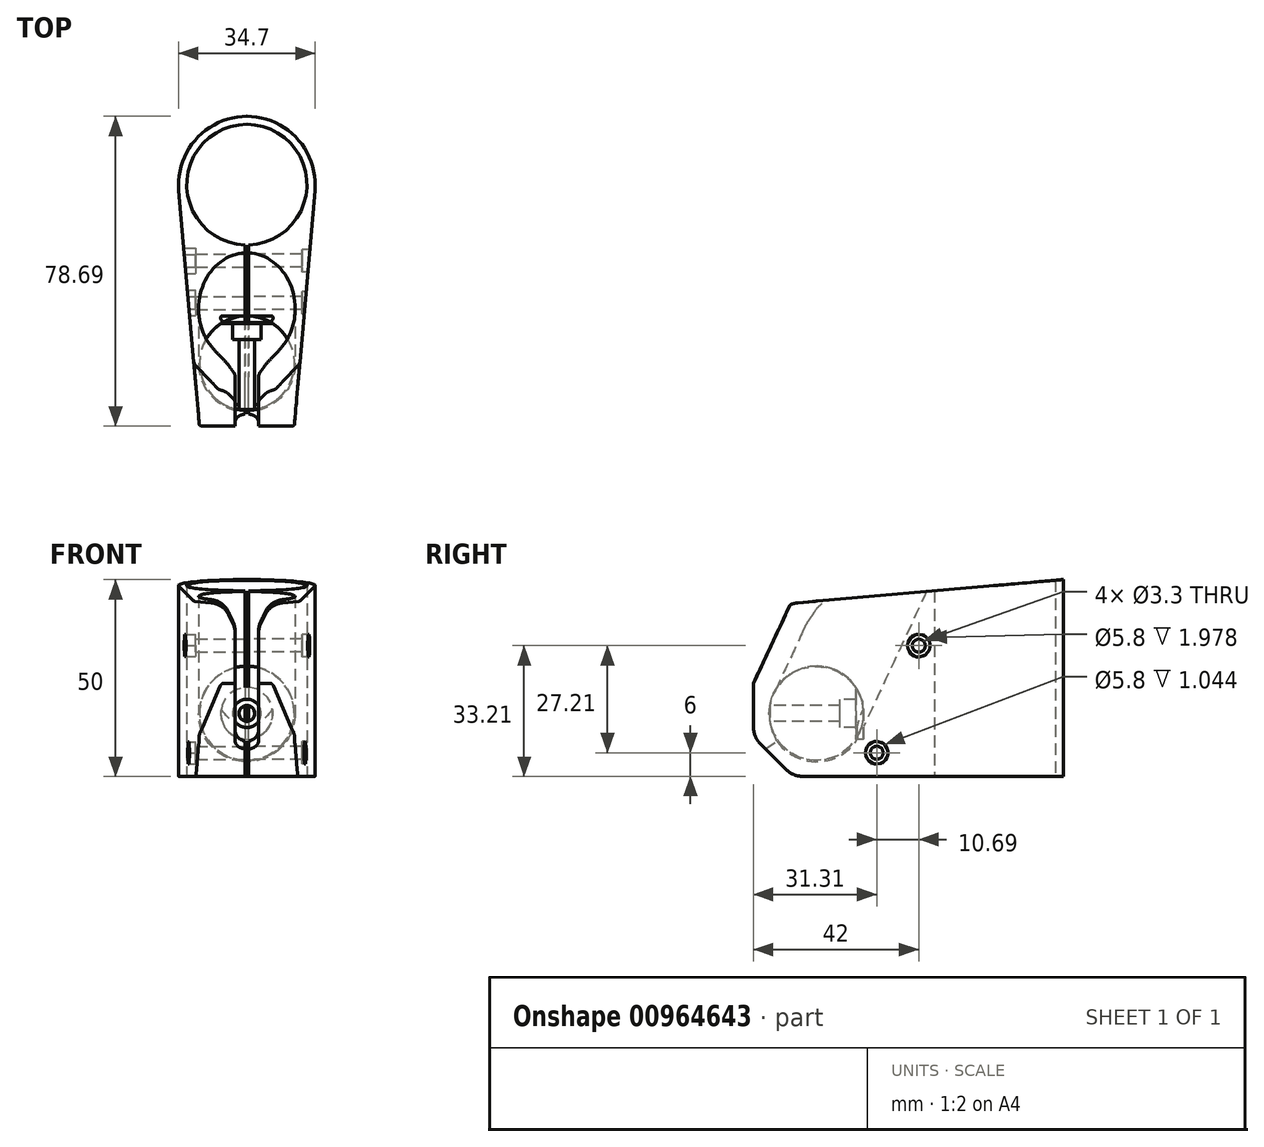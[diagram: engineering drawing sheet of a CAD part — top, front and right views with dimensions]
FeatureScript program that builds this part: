
annotation { "Feature Type Name" : "Feature", "Feature Type Description" : "" }
export const myFeature = defineFeature(function(context is Context, id is Id, definition is map)
    precondition{}
    {
        {
            var Q0;
            Q0=qCreatedBy(makeId("Top.planeOp"),FACE);
            var sketch = newSketch(context, id + "F0", { "sketchPlane" : qUnion([Q0])});
            skCircle(sketch, "E0", {"center": v(0, 0) * mm, "radius": 15.35 * mm, "construction": true});
            skSolve(sketch);
        }
        {
            var Q0;
            Q0=qCreatedBy(makeId("Top.planeOp"),FACE);
            var sketch = newSketch(context, id + "F1", { "sketchPlane" : qUnion([Q0])});
            skArc(sketch, "E1", {"start": v(0.5, -15.34) * mm, "mid": v(15.35, 0.25) * mm, "end": v(0, 15.35) * mm});
            skLineSegment(sketch, "E2", {"start": v(0.5, -15.34) * mm, "end": v(0.5, -61.34) * mm});
            skLineSegment(sketch, "E3", {"start": v(0.5, -61.34) * mm, "end": v(12.05, -61.34) * mm});
            skLineSegment(sketch, "E4", {"start": v(12.05, -61.34) * mm, "end": v(17.28, -1.51) * mm});
            skLineSegment(sketch, "E5", {"start": v(0, 0) * mm, "end": v(0, 15.35) * mm, "construction": true});
            skArc(sketch, "E6", {"start": v(17.28, -1.51) * mm, "mid": v(12.8, 11.72) * mm, "end": v(0, 17.35) * mm});
            skLineSegment(sketch, "E7", {"start": v(0, 15.35) * mm, "end": v(0, 17.35) * mm});
            skSolve(sketch);
        }
        {
            var Q0;
            Q0=qSketchRegion(id+"F1",true);
            extrude(context, id + "F2", {"entities" : qUnion([Q0]), "depth" : 50 * mm});
        }
        {
            var Q0;
            Q0=qCreatedBy(makeId("Right.planeOp"),FACE);
            var sketch = newSketch(context, id + "F3", { "sketchPlane" : qUnion([Q0])});
            skLineSegment(sketch, "E8", {"start": v(-22.2, 65.65) * mm, "end": v(-50.54, 4.85) * mm});
            skArc(sketch, "E9", {"start": v(-56.49, 21.2) * mm, "mid": v(-56.9, 11.8) * mm, "end": v(-50.54, 4.85) * mm});
            skLineSegment(sketch, "E10", {"start": v(-56.49, 21.2) * mm, "end": v(-33.34, 70.84) * mm});
            skLineSegment(sketch, "E11", {"start": v(-33.34, 70.84) * mm, "end": v(-22.2, 65.65) * mm});
            skSolve(sketch);
        }
        {
            var Q0;
            Q0=qSketchRegion(id+"F3",true);
            var Q1;
            Q1=sQuery(id+"F3.wireOp",EDGE,"E8");
            revolve(context, id + "F4", {"operationType" : NewBodyOperationType.REMOVE, "entities" : qUnion([Q0]), "axis" : qUnion([Q1]), "revolveType" : RevolveType.FULL});
        }
        {
            var Q0;
            Q0=makeQuery(id+"F2.opExtrude","CAP_EDGE",EDGE,{"disambiguationData":[OSD([sQuery(id+"F1.wireOp",EDGE,"E3")])],"isStart":true});
            chamfer(context, id + "F5", {"entities" : qUnion([Q0]), "width" : 10 * mm, "tangentPropagation" : true});
        }
        {
            var Q0;
            Q0=qCreatedBy(makeId("Right.planeOp"),FACE);
            var sketch = newSketch(context, id + "F6", { "sketchPlane" : qUnion([Q0])});
            skCircle(sketch, "E12", {"center": v(-19.34, 33.21) * mm, "radius": 1.65 * mm});
            skCircle(sketch, "E13", {"center": v(-30.03, 6) * mm, "radius": 1.65 * mm});
            skLineSegment(sketch, "E14", {"start": v(-30.03, 6) * mm, "end": v(-19.34, 33.21) * mm, "construction": true});
            skLineSegment(sketch, "E15", {"start": v(-30.03, 6) * mm, "end": v(-30.03, 0) * mm, "construction": true});
            skLineSegment(sketch, "E16", {"start": v(-30.03, 6) * mm, "end": v(-35.05, 9.28) * mm, "construction": true});
            skLineSegment(sketch, "E17", {"start": v(-19.34, 33.21) * mm, "end": v(-22.97, 34.9) * mm, "construction": true});
            skLineSegment(sketch, "E18", {"start": v(-19.34, 33.21) * mm, "end": v(-15.34, 33.21) * mm, "construction": true});
            skLineSegment(sketch, "E19", {"start": v(-35.05, 9.28) * mm, "end": v(-31.35, 14.95) * mm, "construction": true});
            skSolve(sketch);
        }
        {
            var Q0;
            Q0=qSketchRegion(id+"F6",true);
            extrude(context, id + "F7", {"entities" : qUnion([Q0]), "operationType" : NewBodyOperationType.REMOVE, "endBound" : BoundingType.THROUGH_ALL, "depth" : 25 * mm});
        }
        {
            var Q0;
            Q0=qCreatedBy(makeId("Right.planeOp"),FACE);
            var sketch = newSketch(context, id + "F8", { "sketchPlane" : qUnion([Q0])});
            skLineSegment(sketch, "E20", {"start": v(-61.34, 50) * mm, "end": v(-49.05, 50) * mm});
            skLineSegment(sketch, "E21", {"start": v(-49.05, 50) * mm, "end": v(-61.34, 23.64) * mm});
            skLineSegment(sketch, "E22", {"start": v(-61.34, 23.64) * mm, "end": v(-61.34, 50) * mm});
            skLineSegment(sketch, "E23", {"start": v(-43.05, 50) * mm, "end": v(-49.05, 50) * mm, "construction": true});
            skSolve(sketch);
        }
        {
            var Q0;
            Q0=qSketchRegion(id+"F8",true);
            extrude(context, id + "F9", {"entities" : qUnion([Q0]), "operationType" : NewBodyOperationType.REMOVE, "endBound" : BoundingType.THROUGH_ALL, "depth" : 25 * mm});
        }
        {
            var Q0;
            Q0=qCreatedBy(makeId("Right.planeOp"),FACE);
            var sketch = newSketch(context, id + "F10", { "sketchPlane" : qUnion([Q0])});
            skLineSegment(sketch, "E24", {"start": v(-29.49, 50) * mm, "end": v(-45.34, 16) * mm});
            skLineSegment(sketch, "E25", {"start": v(-45.34, 16) * mm, "end": v(-74.39, -4.34) * mm});
            skLineSegment(sketch, "E26", {"start": v(-74.39, -4.34) * mm, "end": v(-49.05, 50) * mm});
            skLineSegment(sketch, "E27", {"start": v(-49.05, 50) * mm, "end": v(-29.49, 50) * mm});
            skSolve(sketch);
        }
        {
            var Q0;
            Q0=qSketchRegion(id+"F10",true);
            extrude(context, id + "F11", {"entities" : qUnion([Q0]), "operationType" : NewBodyOperationType.REMOVE, "endBound" : BoundingType.SYMMETRIC, "depth" : 6 * mm});
        }
        {
            var Q0;
            Q0=makeQuery(id+"F11.boolean.opBoolean","COPY",EDGE,{"derivedFrom":makeQuery(id+"F11.opExtrude","CAP_EDGE",EDGE,{"disambiguationData":[OSD([sQuery(id+"F10.wireOp",EDGE,"E25")])],"isStart":false})});
            fillet(context, id + "F12", {"entities" : qUnion([Q0]), "radius" : 3 * mm, "tangentPropagation" : true, "allowEdgeOverflow" : false});
        }
        {
            var Q0;
            Q0=makeQuery(id+"F9.boolean.opBoolean","COPY",EDGE,{"derivedFrom":makeQuery(id+"F9.opExtrude","SWEPT_EDGE",EDGE,{"disambiguationData":[OSD([sQuery(id+"F8.wireOp",EDGE,"E21"),sQuery(id+"F8.wireOp",EDGE,"E22")])]})});
            var Q1;
            {var subQ0=sQuery(id+"F1.wireOp",EDGE,"E3");Q1=makeQuery(id+"F5.opChamfer","BLEND_EDGE",EDGE,{"blendedFrom":[makeQuery(id+"F2.opExtrude","CAP_EDGE",EDGE,{"disambiguationData":[OSD([subQ0])],"isStart":true}),makeQuery(id+"F2.opExtrude","SWEPT_FACE",FACE,{"disambiguationData":[OSD([subQ0])]})],"blendedInto":[makeQuery(id+"F2.opExtrude","SWEPT_FACE",FACE,{"disambiguationData":[OSD([subQ0])]})]});}
            var Q2;
            {var subQ0=sQuery(id+"F1.wireOp",EDGE,"E3");Q2=makeQuery(id+"F5.opChamfer","BLEND_EDGE",EDGE,{"blendedFrom":[makeQuery(id+"F2.opExtrude","CAP_EDGE",EDGE,{"disambiguationData":[OSD([subQ0])],"isStart":true}),makeQuery(id+"F2.opExtrude","CAP_FACE",FACE,{"disambiguationData":[OSD([sQuery(id+"F1.wireOp",EDGE,"E1"),sQuery(id+"F1.wireOp",EDGE,"E2"),subQ0,sQuery(id+"F1.wireOp",EDGE,"E4"),sQuery(id+"F1.wireOp",EDGE,"E6"),sQuery(id+"F1.wireOp",EDGE,"E7")])],"isStart":true})],"blendedInto":[makeQuery(id+"F2.opExtrude","CAP_FACE",FACE,{"disambiguationData":[OSD([sQuery(id+"F1.wireOp",EDGE,"E1"),sQuery(id+"F1.wireOp",EDGE,"E2"),subQ0,sQuery(id+"F1.wireOp",EDGE,"E4"),sQuery(id+"F1.wireOp",EDGE,"E6"),sQuery(id+"F1.wireOp",EDGE,"E7")])],"isStart":true})]});}
            fillet(context, id + "F13", {"entities" : qUnion([Q0, Q1, Q2]), "radius" : 6 * mm, "tangentPropagation" : true, "allowEdgeOverflow" : false});
        }
        {
            var Q0;
            Q0=makeQuery(id+"F2.opExtrude","SWEPT_BODY",BODY,{"disambiguationData":[OSD([sQuery(id+"F1.wireOp",EDGE,"E1"),sQuery(id+"F1.wireOp",EDGE,"E2"),sQuery(id+"F1.wireOp",EDGE,"E3"),sQuery(id+"F1.wireOp",EDGE,"E4"),sQuery(id+"F1.wireOp",EDGE,"E6"),sQuery(id+"F1.wireOp",EDGE,"E7")])]});
            var Q1;
            Q1=makeQuery(id+"F2.opExtrude","SWEPT_FACE",FACE,{"disambiguationData":[OSD([sQuery(id+"F1.wireOp",EDGE,"E7")])]});
            mirror(context, id + "F14", {"operationType" : NewBodyOperationType.ADD, "entities" : qUnion([Q0]), "mirrorPlane" : qUnion([Q1])});
        }
        {
            var Q0;
            Q0=makeQuery(id+"F14.opPattern","COPY",EDGE,{"derivedFrom":makeQuery(id+"F9.boolean.opBoolean","INTERSECT",EDGE,{"derivedFrom":[makeQuery(id+"F2.opExtrude","SWEPT_FACE",FACE,{"disambiguationData":[OSD([sQuery(id+"F1.wireOp",EDGE,"E4")])]}),makeQuery(id+"F9.opExtrude","SWEPT_FACE",FACE,{"disambiguationData":[OSD([sQuery(id+"F8.wireOp",EDGE,"E21")])]})]}),"instanceName":"1"});
            var Q1;
            Q1=makeQuery(id+"F9.boolean.opBoolean","INTERSECT",EDGE,{"derivedFrom":[makeQuery(id+"F2.opExtrude","SWEPT_FACE",FACE,{"disambiguationData":[OSD([sQuery(id+"F1.wireOp",EDGE,"E4")])]}),makeQuery(id+"F9.opExtrude","SWEPT_FACE",FACE,{"disambiguationData":[OSD([sQuery(id+"F8.wireOp",EDGE,"E21")])]})]});
            chamfer(context, id + "F15", {"entities" : qUnion([Q0, Q1]), "width" : 6 * mm});
        }
        {
            var Q0;
            Q0=qCreatedBy(makeId("Right.planeOp"),FACE);
            var sketch = newSketch(context, id + "F16", { "sketchPlane" : qUnion([Q0])});
            skLineSegment(sketch, "E28", {"start": v(-34.47, 10.93) * mm, "end": v(-56.22, 21.07) * mm});
            skArc(sketch, "E29", {"start": v(-56.22, 21.07) * mm, "mid": v(-50.41, 5.12) * mm, "end": v(-34.47, 10.93) * mm});
            skSolve(sketch);
        }
        {
            var Q0;
            Q0=qSketchRegion(id+"F16",true);
            var Q1;
            Q1=sQuery(id+"F16.wireOp",EDGE,"E28");
            revolve(context, id + "F17", {"entities" : qUnion([Q0]), "axis" : qUnion([Q1]), "revolveType" : RevolveType.FULL});
        }
        {
            var Q0;
            {var subQ0=makeQuery(id+"F2.opExtrude","CAP_EDGE",EDGE,{"disambiguationData":[OSD([sQuery(id+"F1.wireOp",EDGE,"E6")])],"isStart":true});Q0=makeQuery(id+"F14.boolean.opBoolean","MERGE",EDGE,{"derivedFrom":[subQ0,makeQuery(id+"F14.opPattern","COPY",EDGE,{"derivedFrom":subQ0,"instanceName":"1"})]});}
            var Q1;
            {var subQ0=makeQuery(id+"F2.opExtrude","SWEPT_FACE",FACE,{"disambiguationData":[OSD([sQuery(id+"F1.wireOp",EDGE,"E4")])]});Q1=makeQuery(id+"F15.opChamfer","BLEND_EDGE",EDGE,{"blendedFrom":[makeQuery(id+"F14.opPattern","COPY",EDGE,{"derivedFrom":makeQuery(id+"F9.boolean.opBoolean","INTERSECT",EDGE,{"derivedFrom":[subQ0,makeQuery(id+"F9.opExtrude","SWEPT_FACE",FACE,{"disambiguationData":[OSD([sQuery(id+"F8.wireOp",EDGE,"E21")])]})]}),"instanceName":"1"}),makeQuery(id+"F14.opPattern","COPY",FACE,{"derivedFrom":subQ0,"instanceName":"1"})],"blendedInto":[makeQuery(id+"F14.opPattern","COPY",FACE,{"derivedFrom":subQ0,"instanceName":"1"})]});}
            var Q2;
            {var subQ0=makeQuery(id+"F9.opExtrude","SWEPT_FACE",FACE,{"disambiguationData":[OSD([sQuery(id+"F8.wireOp",EDGE,"E21")])]});Q2=makeQuery(id+"F15.opChamfer","BLEND_EDGE",EDGE,{"blendedFrom":[makeQuery(id+"F14.opPattern","COPY",EDGE,{"derivedFrom":makeQuery(id+"F9.boolean.opBoolean","INTERSECT",EDGE,{"derivedFrom":[makeQuery(id+"F2.opExtrude","SWEPT_FACE",FACE,{"disambiguationData":[OSD([sQuery(id+"F1.wireOp",EDGE,"E4")])]}),subQ0]}),"instanceName":"1"}),makeQuery(id+"F14.opPattern","COPY",FACE,{"derivedFrom":makeQuery(id+"F9.boolean.opBoolean","COPY",FACE,{"derivedFrom":subQ0}),"instanceName":"1"})],"blendedInto":[makeQuery(id+"F14.opPattern","COPY",FACE,{"derivedFrom":makeQuery(id+"F9.boolean.opBoolean","COPY",FACE,{"derivedFrom":subQ0}),"instanceName":"1"})]});}
            var Q3;
            {var subQ0=makeQuery(id+"F9.opExtrude","SWEPT_FACE",FACE,{"disambiguationData":[OSD([sQuery(id+"F8.wireOp",EDGE,"E21")])]});Q3=makeQuery(id+"F15.opChamfer","BLEND_EDGE",EDGE,{"blendedFrom":[makeQuery(id+"F9.boolean.opBoolean","INTERSECT",EDGE,{"derivedFrom":[makeQuery(id+"F2.opExtrude","SWEPT_FACE",FACE,{"disambiguationData":[OSD([sQuery(id+"F1.wireOp",EDGE,"E4")])]}),subQ0]}),makeQuery(id+"F9.boolean.opBoolean","COPY",FACE,{"derivedFrom":subQ0})],"blendedInto":[makeQuery(id+"F9.boolean.opBoolean","COPY",FACE,{"derivedFrom":subQ0})]});}
            var Q4;
            {var subQ0=makeQuery(id+"F2.opExtrude","SWEPT_FACE",FACE,{"disambiguationData":[OSD([sQuery(id+"F1.wireOp",EDGE,"E4")])]});Q4=makeQuery(id+"F15.opChamfer","BLEND_EDGE",EDGE,{"blendedFrom":[makeQuery(id+"F9.boolean.opBoolean","INTERSECT",EDGE,{"derivedFrom":[subQ0,makeQuery(id+"F9.opExtrude","SWEPT_FACE",FACE,{"disambiguationData":[OSD([sQuery(id+"F8.wireOp",EDGE,"E21")])]})]}),subQ0],"blendedInto":[subQ0]});}
            fillet(context, id + "F18", {"entities" : qUnion([Q0, Q1, Q2, Q3, Q4]), "radius" : 1 * mm, "tangentPropagation" : true, "rho" : .2, "crossSection" : FilletCrossSection.CONIC, "allowEdgeOverflow" : false});
        }
        {
            var Q0;
            Q0=qCreatedBy(makeId("Right.planeOp"),FACE);
            var sketch = newSketch(context, id + "F19", { "sketchPlane" : qUnion([Q0])});
            skLineSegment(sketch, "E30", {"start": v(-33.34, 16) * mm, "end": v(-57.34, 16) * mm});
            skLineSegment(sketch, "E31", {"start": v(-57.34, 16) * mm, "end": v(-57.34, 18) * mm});
            skLineSegment(sketch, "E32", {"start": v(-57.34, 18) * mm, "end": v(-39.34, 18) * mm});
            skLineSegment(sketch, "E33", {"start": v(-39.34, 18) * mm, "end": v(-39.34, 19.6) * mm});
            skLineSegment(sketch, "E34", {"start": v(-33.34, 19.6) * mm, "end": v(-33.34, 16) * mm});
            skCircle(sketch, "E35", {"center": v(-45.34, 16) * mm, "radius": 12 * mm, "construction": true});
            skLineSegment(sketch, "E36", {"start": v(-39.34, 19.6) * mm, "end": v(-35.34, 19.6) * mm});
            skLineSegment(sketch, "E37", {"start": v(-35.34, 19.6) * mm, "end": v(-35.34, 22.63) * mm});
            skLineSegment(sketch, "E38", {"start": v(-35.34, 22.63) * mm, "end": v(-33.34, 22.63) * mm});
            skLineSegment(sketch, "E39", {"start": v(-33.34, 22.63) * mm, "end": v(-33.34, 19.6) * mm});
            skSolve(sketch);
        }
        {
            var Q0;
            Q0=qSketchRegion(id+"F19",true);
            var Q1;
            Q1=sQuery(id+"F19.wireOp",EDGE,"E30");
            revolve(context, id + "F20", {"operationType" : NewBodyOperationType.REMOVE, "entities" : qUnion([Q0]), "axis" : qUnion([Q1]), "revolveType" : RevolveType.FULL, "oppositeDirection" : true});
        }
        {
            var Q0;
            Q0=qCreatedBy(makeId("Right.planeOp"),FACE);
            var sketch = newSketch(context, id + "F21", { "sketchPlane" : qUnion([Q0])});
            skLineSegment(sketch, "E40", {"start": v(17.35, 50) * mm, "end": v(-84.6, 50) * mm});
            skLineSegment(sketch, "E41", {"start": v(-84.6, 50) * mm, "end": v(-84.6, 41.08) * mm});
            skLineSegment(sketch, "E42", {"start": v(-84.6, 41.08) * mm, "end": v(17.35, 50) * mm});
            skSolve(sketch);
        }
        {
            var Q0;
            Q0=qSketchRegion(id+"F21",true);
            extrude(context, id + "F22", {"entities" : qUnion([Q0]), "operationType" : NewBodyOperationType.REMOVE, "endBound" : BoundingType.THROUGH_ALL, "oppositeDirection" : true, "depth" : 25 * mm, "hasSecondDirection" : true, "secondDirectionBound" : SecondDirectionBoundingType.THROUGH_ALL, "secondDirectionOppositeDirection" : false, "secondDirectionDepth" : 25 * mm});
        }
        {
            var Q0;
            Q0=makeQuery(id+"F22.boolean.opBoolean","INTERSECT",EDGE,{"derivedFrom":[makeQuery(id+"F11.boolean.opBoolean","COPY",FACE,{"derivedFrom":makeQuery(id+"F11.opExtrude","CAP_FACE",FACE,{"disambiguationData":[OSD([sQuery(id+"F10.wireOp",EDGE,"E24"),sQuery(id+"F10.wireOp",EDGE,"E25"),sQuery(id+"F10.wireOp",EDGE,"E26"),sQuery(id+"F10.wireOp",EDGE,"E27")])],"isStart":false})}),makeQuery(id+"F22.opExtrude","SWEPT_FACE",FACE,{"disambiguationData":[OSD([sQuery(id+"F21.wireOp",EDGE,"E42")])]})]});
            var Q1;
            Q1=makeQuery(id+"F22.boolean.opBoolean","INTERSECT",EDGE,{"derivedFrom":[makeQuery(id+"F14.opPattern","COPY",FACE,{"derivedFrom":makeQuery(id+"F11.boolean.opBoolean","COPY",FACE,{"derivedFrom":makeQuery(id+"F11.opExtrude","CAP_FACE",FACE,{"disambiguationData":[OSD([sQuery(id+"F10.wireOp",EDGE,"E24"),sQuery(id+"F10.wireOp",EDGE,"E25"),sQuery(id+"F10.wireOp",EDGE,"E26"),sQuery(id+"F10.wireOp",EDGE,"E27")])],"isStart":false})}),"instanceName":"1"}),makeQuery(id+"F22.opExtrude","SWEPT_FACE",FACE,{"disambiguationData":[OSD([sQuery(id+"F21.wireOp",EDGE,"E42")])]})]});
            chamfer(context, id + "F23", {"entities" : qUnion([Q0, Q1]), "chamferType" : ChamferType.TWO_OFFSETS, "width1" : 6 * mm, "oppositeDirection" : false, "width2" : 3 * mm, "tangentPropagation" : true});
        }
        {
            var Q0;
            {var subQ0=makeQuery(id+"F22.opExtrude","SWEPT_FACE",FACE,{"disambiguationData":[OSD([sQuery(id+"F21.wireOp",EDGE,"E42")])]});Q0=makeQuery(id+"F23.opChamfer","BLEND_EDGE",EDGE,{"blendedFrom":[makeQuery(id+"F22.boolean.opBoolean","INTERSECT",EDGE,{"derivedFrom":[makeQuery(id+"F11.boolean.opBoolean","COPY",FACE,{"derivedFrom":makeQuery(id+"F11.opExtrude","CAP_FACE",FACE,{"disambiguationData":[OSD([sQuery(id+"F10.wireOp",EDGE,"E24"),sQuery(id+"F10.wireOp",EDGE,"E25"),sQuery(id+"F10.wireOp",EDGE,"E26"),sQuery(id+"F10.wireOp",EDGE,"E27")])],"isStart":false})}),subQ0]}),makeQuery(id+"F22.boolean.opBoolean","COPY",FACE,{"derivedFrom":subQ0})],"blendedInto":[makeQuery(id+"F22.boolean.opBoolean","COPY",FACE,{"derivedFrom":subQ0})]});}
            var Q1;
            {var subQ0=makeQuery(id+"F22.opExtrude","SWEPT_FACE",FACE,{"disambiguationData":[OSD([sQuery(id+"F21.wireOp",EDGE,"E42")])]});Q1=makeQuery(id+"F23.opChamfer","BLEND_EDGE",EDGE,{"blendedFrom":[makeQuery(id+"F22.boolean.opBoolean","INTERSECT",EDGE,{"derivedFrom":[makeQuery(id+"F14.opPattern","COPY",FACE,{"derivedFrom":makeQuery(id+"F11.boolean.opBoolean","COPY",FACE,{"derivedFrom":makeQuery(id+"F11.opExtrude","CAP_FACE",FACE,{"disambiguationData":[OSD([sQuery(id+"F10.wireOp",EDGE,"E24"),sQuery(id+"F10.wireOp",EDGE,"E25"),sQuery(id+"F10.wireOp",EDGE,"E26"),sQuery(id+"F10.wireOp",EDGE,"E27")])],"isStart":false})}),"instanceName":"1"}),subQ0]}),makeQuery(id+"F22.boolean.opBoolean","COPY",FACE,{"derivedFrom":subQ0})],"blendedInto":[makeQuery(id+"F22.boolean.opBoolean","COPY",FACE,{"derivedFrom":subQ0})]});}
            var Q2;
            {var subQ0=makeQuery(id+"F11.boolean.opBoolean","COPY",FACE,{"derivedFrom":makeQuery(id+"F11.opExtrude","CAP_FACE",FACE,{"disambiguationData":[OSD([sQuery(id+"F10.wireOp",EDGE,"E24"),sQuery(id+"F10.wireOp",EDGE,"E25"),sQuery(id+"F10.wireOp",EDGE,"E26"),sQuery(id+"F10.wireOp",EDGE,"E27")])],"isStart":false})});Q2=makeQuery(id+"F23.opChamfer","BLEND_EDGE",EDGE,{"blendedFrom":[makeQuery(id+"F22.boolean.opBoolean","INTERSECT",EDGE,{"derivedFrom":[subQ0,makeQuery(id+"F22.opExtrude","SWEPT_FACE",FACE,{"disambiguationData":[OSD([sQuery(id+"F21.wireOp",EDGE,"E42")])]})]}),subQ0],"blendedInto":[subQ0]});}
            var Q3;
            {var subQ0=makeQuery(id+"F14.opPattern","COPY",FACE,{"derivedFrom":makeQuery(id+"F11.boolean.opBoolean","COPY",FACE,{"derivedFrom":makeQuery(id+"F11.opExtrude","CAP_FACE",FACE,{"disambiguationData":[OSD([sQuery(id+"F10.wireOp",EDGE,"E24"),sQuery(id+"F10.wireOp",EDGE,"E25"),sQuery(id+"F10.wireOp",EDGE,"E26"),sQuery(id+"F10.wireOp",EDGE,"E27")])],"isStart":false})}),"instanceName":"1"});Q3=makeQuery(id+"F23.opChamfer","BLEND_EDGE",EDGE,{"blendedFrom":[makeQuery(id+"F22.boolean.opBoolean","INTERSECT",EDGE,{"derivedFrom":[subQ0,makeQuery(id+"F22.opExtrude","SWEPT_FACE",FACE,{"disambiguationData":[OSD([sQuery(id+"F21.wireOp",EDGE,"E42")])]})]}),subQ0],"blendedInto":[subQ0]});}
            fillet(context, id + "F24", {"entities" : qUnion([Q0, Q1, Q2, Q3]), "radius" : 5 * mm, "tangentPropagation" : true, "allowEdgeOverflow" : false});
        }
        {
            var Q0;
            Q0=qCreatedBy(makeId("Right.planeOp"),FACE);
            cPlane(context, id + "F25", {"entities" : qUnion([Q0]), "cplaneType" : CPlaneType.OFFSET, "offset" : 14 * mm, "width" : 150 * mm, "height" : 150 * mm});
        }
        {
            var Q0;
            Q0=qCreatedBy(makeId("Right.planeOp"),FACE);
            cPlane(context, id + "F26", {"entities" : qUnion([Q0]), "cplaneType" : CPlaneType.OFFSET, "offset" : 13 * mm, "oppositeDirection" : true, "width" : 150 * mm, "height" : 150 * mm});
        }
        {
            var Q0;
            Q0=qCreatedBy(id+"F25.planeOp",FACE);
            var sketch = newSketch(context, id + "F27", { "sketchPlane" : qUnion([Q0])});
            skCircle(sketch, "E43", {"center": v(-19.34, 33.21) * mm, "radius": 2.9 * mm});
            skCircle(sketch, "E44", {"center": v(-30.03, 6) * mm, "radius": 2.9 * mm});
            skSolve(sketch);
        }
        {
            var Q0;
            Q0=qSketchRegion(id+"F27",true);
            extrude(context, id + "F28", {"entities" : qUnion([Q0]), "operationType" : NewBodyOperationType.REMOVE, "endBound" : BoundingType.THROUGH_ALL, "depth" : 25 * mm});
        }
        {
            var Q0;
            Q0=qCreatedBy(id+"F26.planeOp",FACE);
            var sketch = newSketch(context, id + "F29", { "sketchPlane" : qUnion([Q0])});
            skCircle(sketch, "E45", {"center": v(-19.34, 33.21) * mm, "radius": 3.23 * mm, "construction": true});
            skLineSegment(sketch, "E46", {"start": v(-17.73, 36.01) * mm, "end": v(-20.96, 36.01) * mm});
            skLineSegment(sketch, "E47", {"start": v(-20.96, 36.01) * mm, "end": v(-22.58, 33.21) * mm});
            skLineSegment(sketch, "E48", {"start": v(-22.58, 33.21) * mm, "end": v(-20.96, 30.41) * mm});
            skLineSegment(sketch, "E49", {"start": v(-20.96, 30.41) * mm, "end": v(-17.73, 30.41) * mm});
            skLineSegment(sketch, "E50", {"start": v(-17.73, 30.41) * mm, "end": v(-16.1, 33.21) * mm});
            skLineSegment(sketch, "E51", {"start": v(-16.1, 33.21) * mm, "end": v(-17.73, 36.01) * mm});
            skLineSegment(sketch, "E52", {"start": v(-31.64, 3.2) * mm, "end": v(-28.41, 3.2) * mm});
            skLineSegment(sketch, "E53", {"start": v(-26.8, 6) * mm, "end": v(-28.41, 8.8) * mm});
            skLineSegment(sketch, "E54", {"start": v(-33.26, 6) * mm, "end": v(-31.64, 3.2) * mm});
            skLineSegment(sketch, "E55", {"start": v(-28.41, 3.2) * mm, "end": v(-26.8, 6) * mm});
            skLineSegment(sketch, "E56", {"start": v(-31.64, 8.8) * mm, "end": v(-33.26, 6) * mm});
            skCircle(sketch, "E57", {"center": v(-30.03, 6) * mm, "radius": 3.23 * mm, "construction": true});
            skLineSegment(sketch, "E58", {"start": v(-28.41, 8.8) * mm, "end": v(-31.64, 8.8) * mm});
            skSolve(sketch);
        }
        {
            var Q0;
            Q0=qSketchRegion(id+"F29",true);
            extrude(context, id + "F30", {"entities" : qUnion([Q0]), "operationType" : NewBodyOperationType.REMOVE, "endBound" : BoundingType.THROUGH_ALL, "oppositeDirection" : true, "depth" : 25 * mm});
        }
    });
